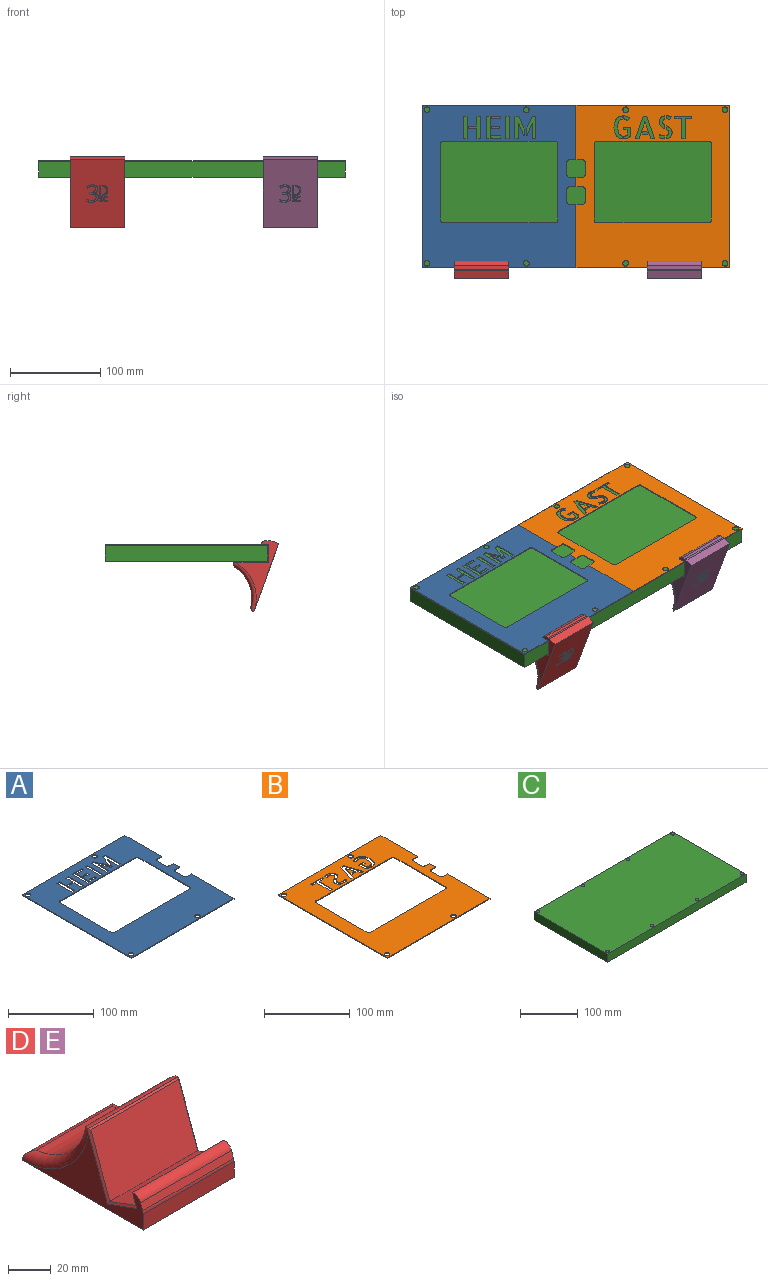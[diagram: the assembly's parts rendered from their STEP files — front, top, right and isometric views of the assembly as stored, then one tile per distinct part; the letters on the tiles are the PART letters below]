
ASSEMBLY  parts=5 mates=4
PART A: 78 faces, bbox 170x180x1 mm
  f0: plane 4.07x1mm, normal (0,-1,0), area 4.1mm2, adj f1,f67,f68,f69
  f1: plane 24.99x1mm, normal (-1,0,0), area 25mm2, adj f0,f2,f68,f69
  f2: plane 4.07x1mm, normal (0,1,0), area 4.1mm2, adj f1,f3,f68,f69
  f3: plane 11.26x1mm, normal (1,0,0), area 11.3mm2, adj f2,f4,f68,f69
  f4: plane 9.43x1mm, normal (0,1,0), area 9.4mm2, adj f3,f5,f68,f69
  f5: plane 2.78x1mm, normal (1,0,0), area 2.8mm2, adj f4,f6,f68,f69
  f6: plane 9.43x1mm, normal (0,-1,0), area 9.4mm2, adj f5,f67,f68,f69
  f7: plane 24.99x1mm, normal (1,0,0), area 25mm2, adj f8,f53,f68,f69
  f8: plane 4.13x1mm, normal (0,-1,0), area 4.1mm2, adj f7,f9,f68,f69
  f9: plane 24.99x1mm, normal (-1,0,0), area 25mm2, adj f8,f53,f68,f69
  f10: plane 24.99x1mm, normal (1,0,0), area 25mm2, adj f11,f54,f68,f69
  f11: plane 4.13x1mm, normal (0,-1,0), area 4.1mm2, adj f10,f12,f68,f69
  f12: plane 24.99x1mm, normal (-1,0,0), area 25mm2, adj f11,f54,f68,f69
  f13: plane 2.78x1mm, normal (-1,0,0), area 2.8mm2, adj f14,f55,f68,f69
  f14: plane 9.05x1mm, normal (0,1,0), area 9mm2, adj f13,f15,f68,f69
  f15: plane 2.78x1mm, normal (1,0,0), area 2.8mm2, adj f14,f55,f68,f69
  f16: plane 3.09x1mm, normal (1,0,0), area 3.1mm2, adj f17,f56,f68,f69
  f17: plane 10.1x1mm, normal (0,-1,0), area 10.1mm2, adj f16,f18,f68,f69
  f18: plane 3.09x1mm, normal (-1,0,0), area 3.1mm2, adj f17,f56,f68,f69
  f19: plane 10.1x1mm, normal (0,-1,0), area 10.1mm2, adj f20,f57,f68,f69
  f20: plane 3.08x1mm, normal (-1,0,0), area 3.1mm2, adj f19,f21,f68,f69
  f21: plane 10.1x1mm, normal (0,1,0), area 10.1mm2, adj f20,f57,f68,f69
  f22: plane 24.99x1mm, normal (-1,0,0), area 25mm2, adj f23,f58,f68,f69
  f23: plane 4.13x1mm, normal (0,1,0), area 4.1mm2, adj f22,f24,f68,f69
  f24: plane 24.99x1mm, normal (1,0,0), area 25mm2, adj f23,f58,f68,f69
  f25: plane 24.99x1mm, normal (1,0,0), area 25mm2, adj f26,f59,f68,f69
  f26: plane 4.14x1mm, normal (0,-1,0), area 4.1mm2, adj f25,f27,f68,f69
  f27: plane 15.42x6.71mm, normal (-0.92,-0.4,0), area 16.8mm2, adj f26,f28,f68,f69
  f28: plane 6.28x1mm, normal (-1,0,0), area 6.3mm2, adj f27,f29,f68,f69
  f29: plane 1.09x1mm, normal (0,1,0), area 1.1mm2, adj f28,f30,f68,f69
  f30: plane 13.91x5.63mm, normal (0.93,0.38,0), area 15mm2, adj f29,f31,f68,f69
  f31: plane 17.19x1mm, normal (-1,0,0), area 17.2mm2, adj f30,f59,f68,f69
  f32: plane 15.49x6.72mm, normal (0.92,-0.4,0), area 16.9mm2, adj f33,f60,f68,f69
  f33: plane 4.13x1mm, normal (0,-1,0), area 4.1mm2, adj f32,f34,f68,f69
  f34: plane 24.99x1mm, normal (-1,0,0), area 25mm2, adj f33,f35,f68,f69
  f35: plane 4.13x1mm, normal (0,1,0), area 4.1mm2, adj f34,f36,f68,f69
  f36: plane 17.19x1mm, normal (1,0,0), area 17.2mm2, adj f35,f37,f68,f69
  f37: plane 13.91x5.59mm, normal (-0.93,0.37,0), area 15mm2, adj f36,f38,f68,f69
  f38: plane 1.12x1mm, normal (0,1,0), area 1.1mm2, adj f37,f60,f68,f69
  f39: plane 60x1mm, normal (1,0,0), area 60mm2, adj f40,f65,f68,f69
  f40: plane 170x1mm, normal (0,1,0), area 170mm2, adj f39,f41,f68,f69
  f41: plane 180x1mm, normal (-1,0,0), area 180mm2, adj f40,f42,f68,f69
  f42: plane 170x1mm, normal (0,-1,0), area 170mm2, adj f41,f43,f68,f69
  f43: plane 70x1mm, normal (1,0,0), area 70mm2, adj f42,f44,f68,f69
  f44: plane 7x1mm, normal (0,1,0), area 7mm2, adj f43,f68,f69,f74
  f45: plane 14x1mm, normal (1,0,0), area 14mm2, adj f68,f69,f74,f75
  f46: plane 7x1mm, normal (0,-1,0), area 7mm2, adj f47,f68,f69,f75
  f47: plane 10x1mm, normal (1,0,0), area 10mm2, adj f46,f48,f68,f69
  f48: plane 7x1mm, normal (0,1,0), area 7mm2, adj f47,f68,f69,f76
  f49: plane 14x1mm, normal (1,0,0), area 14mm2, adj f68,f69,f76,f77
  f50: plane 84x1mm, normal (1,0,0), area 84mm2, adj f68,f69,f70,f73
  f51: plane 124x1mm, normal (0,-1,0), area 124mm2, adj f68,f69,f70,f71
  f52: plane 84x1mm, normal (-1,0,0), area 84mm2, adj f68,f69,f71,f72
  f53: plane 4.13x1mm, normal (0,1,0), area 4.1mm2, adj f7,f9,f68,f69
  f54: plane 4.13x1mm, normal (0,1,0), area 4.1mm2, adj f10,f12,f68,f69
  f55: plane 9.05x1mm, normal (0,-1,0), area 9mm2, adj f13,f15,f68,f69
  f56: plane 10.1x1mm, normal (0,1,0), area 10.1mm2, adj f16,f18,f68,f69
  f57: plane 3.08x1mm, normal (1,0,0), area 3.1mm2, adj f19,f21,f68,f69
  f58: plane 4.13x1mm, normal (0,-1,0), area 4.1mm2, adj f22,f24,f68,f69
  f59: plane 4.14x1mm, normal (0,1,0), area 4.1mm2, adj f25,f31,f68,f69
  f60: plane 6.21x1mm, normal (1,0,0), area 6.2mm2, adj f32,f38,f68,f69
  f61: cylinder r=3.25mm len=6.5mm, axis (0,0,-1), area 20.4mm2, adj f68,f69
  f62: cylinder r=3.25mm len=6.5mm, axis (0,0,-1), area 20.4mm2, adj f68,f69
  f63: cylinder r=3.25mm len=6.5mm, axis (0,0,-1), area 20.4mm2, adj f68,f69
  f64: cylinder r=3.25mm len=6.5mm, axis (0,0,-1), area 20.4mm2, adj f68,f69
  f65: plane 7x1mm, normal (0,-1,0), area 7mm2, adj f39,f68,f69,f77
  f66: plane 124x1mm, normal (0,1,0), area 124mm2, adj f68,f69,f72,f73
  f67: plane 10.95x1mm, normal (1,0,0), area 10.9mm2, adj f0,f6,f68,f69
  f68: plane 180x170mm, normal (0,0,1), area 17541mm2, adj f0,f1,f2,f3,f4,f5,f6,f7
  f69: plane 180x170mm, normal (0,0,-1), area 17541mm2, adj f0,f1,f2,f3,f4,f5,f6,f7
  f70: cylinder r=3mm len=3mm, axis (0,0,-1), area 4.7mm2, adj f50,f51,f68,f69
  f71: cylinder r=3mm len=3mm, axis (0,0,1), area 4.7mm2, adj f51,f52,f68,f69
  f72: cylinder r=3mm len=3mm, axis (0,0,-1), area 4.7mm2, adj f52,f66,f68,f69
  f73: cylinder r=3mm len=3mm, axis (0,0,1), area 4.7mm2, adj f50,f66,f68,f69
  f74: cylinder r=3mm len=3mm, axis (0,0,1), area 4.7mm2, adj f44,f45,f68,f69
  f75: cylinder r=3mm len=3mm, axis (0,0,-1), area 4.7mm2, adj f45,f46,f68,f69
  f76: cylinder r=3mm len=3mm, axis (0,0,1), area 4.7mm2, adj f48,f49,f68,f69
  f77: cylinder r=3mm len=3mm, axis (0,0,-1), area 4.7mm2, adj f49,f65,f68,f69
PART B: 140 faces, bbox 170x180x1 mm
  f0: plane 14x1mm, normal (1,0,0), area 14mm2, adj f130,f131,f136,f139
  f1: plane 7x1mm, normal (0,-1,0), area 7mm2, adj f2,f130,f131,f136
  f2: plane 60x1mm, normal (1,0,0), area 60mm2, adj f1,f3,f130,f131
  f3: plane 170x1mm, normal (0,1,0), area 170mm2, adj f2,f4,f130,f131
  f4: plane 180x1mm, normal (-1,0,0), area 180mm2, adj f3,f5,f130,f131
  f5: plane 170x1mm, normal (0,-1,0), area 170mm2, adj f4,f6,f130,f131
  f6: plane 70x1mm, normal (1,0,0), area 70mm2, adj f5,f7,f130,f131
  f7: plane 7x1mm, normal (0,1,0), area 7mm2, adj f6,f130,f131,f137
  f8: plane 14x1mm, normal (1,0,0), area 14mm2, adj f130,f131,f137,f138
  f9: plane 7x1mm, normal (0,-1,0), area 7mm2, adj f10,f130,f131,f138
  f10: plane 10x1mm, normal (1,0,0), area 10mm2, adj f9,f129,f130,f131
  f11: plane 2.78x1mm, normal (1,0,0), area 2.8mm2, adj f12,f118,f130,f131
  f12: plane 19.02x1mm, normal (0,-1,0), area 19mm2, adj f11,f13,f130,f131
  f13: plane 2.78x1mm, normal (-1,0,0), area 2.8mm2, adj f12,f14,f130,f131
  f14: plane 7.46x1mm, normal (0,1,0), area 7.5mm2, adj f13,f15,f130,f131
  f15: plane 22.21x1mm, normal (-1,0,0), area 22.2mm2, adj f14,f16,f130,f131
  f16: plane 4.1x1mm, normal (0,1,0), area 4.1mm2, adj f15,f17,f130,f131
  f17: plane 22.21x1mm, normal (1,0,0), area 22.2mm2, adj f16,f118,f130,f131
  f18: extruded ~2.29x1.09mm, area 2.5mm2, adj f19,f119,f130,f131
  f19: plane 3.97x1mm, normal (-1,0,0), area 4mm2, adj f18,f20,f130,f131
  f20: extruded ~2x1.46mm, area 2.5mm2, adj f19,f21,f130,f131
  f21: extruded ~1.97x1mm, area 2.2mm2, adj f20,f22,f130,f131
  f22: extruded ~3.69x2.78mm, area 5.1mm2, adj f21,f23,f130,f131
  f23: plane 3.26x1mm, normal (-1,0,0), area 3.3mm2, adj f22,f24,f130,f131
  f24: extruded ~2.78x1mm, area 2.9mm2, adj f23,f25,f130,f131
  f25: extruded ~2.05x1.58mm, area 2.6mm2, adj f24,f26,f130,f131
  f26: extruded ~2.09x1.29mm, area 2.5mm2, adj f25,f27,f130,f131
  f27: extruded ~2.37x1mm, area 2.4mm2, adj f26,f28,f130,f131
  f28: extruded ~2.95x1mm, area 3mm2, adj f27,f29,f130,f131
  f29: extruded ~2.02x1.56mm, area 2.6mm2, adj f28,f119,f130,f131
  f30: extruded ~1.2x1mm, area 1.3mm2, adj f31,f120,f130,f131
  f31: plane 2.92x1mm, normal (-0.97,-0.24,0), area 3mm2, adj f30,f32,f130,f131
  f32: extruded ~1.38x1mm, area 1.6mm2, adj f31,f33,f130,f131
  f33: extruded ~1.68x1mm, area 1.8mm2, adj f32,f34,f130,f131
  f34: extruded ~1.75x1mm, area 1.8mm2, adj f33,f35,f130,f131
  f35: extruded ~1.68x1mm, area 1.7mm2, adj f34,f36,f130,f131
  f36: plane 1x0.07mm, normal (0,1,0), area 0.1mm2, adj f35,f37,f130,f131
  f37: plane 3.22x1mm, normal (1,0,0), area 3.2mm2, adj f36,f38,f130,f131
  f38: plane 1x0.1mm, normal (0,-1,0), area 0.1mm2, adj f37,f39,f130,f131
  f39: extruded ~1.46x1mm, area 1.5mm2, adj f38,f40,f130,f131
  f40: extruded ~1.56x1mm, area 1.6mm2, adj f39,f120,f130,f131
  f41: extruded ~2.68x1mm, area 2.7mm2, adj f42,f121,f130,f131
  f42: extruded ~2.68x1mm, area 2.8mm2, adj f41,f43,f130,f131
  f43: extruded ~1.97x1.51mm, area 2.5mm2, adj f42,f44,f130,f131
  f44: extruded ~2.03x1.48mm, area 2.5mm2, adj f43,f45,f130,f131
  f45: extruded ~2.24x1.17mm, area 2.5mm2, adj f44,f46,f130,f131
  f46: plane 3.87x1mm, normal (1,0,0), area 3.9mm2, adj f45,f47,f130,f131
  f47: extruded ~1.8x1.42mm, area 2.3mm2, adj f46,f48,f130,f131
  f48: extruded ~2.14x1mm, area 2.3mm2, adj f47,f49,f130,f131
  f49: extruded ~1.88x1mm, area 2.1mm2, adj f48,f50,f130,f131
  f50: extruded ~1.8x1.3mm, area 2.3mm2, adj f49,f51,f130,f131
  f51: plane 3.56x1mm, normal (1,0,0), area 3.6mm2, adj f50,f52,f130,f131
  f52: extruded ~2.46x1mm, area 2.6mm2, adj f51,f53,f130,f131
  f53: extruded ~2.03x1.42mm, area 2.5mm2, adj f52,f121,f130,f131
  f54: extruded ~1x0.41mm, area 0.5mm2, adj f55,f122,f130,f131
  f55: extruded ~1x0.34mm, area 0.4mm2, adj f54,f56,f130,f131
  f56: extruded ~1x0.76mm, area 0.9mm2, adj f55,f57,f130,f131
  f57: extruded ~1x0.98mm, area 1.1mm2, adj f56,f58,f130,f131
  f58: extruded ~1x0.97mm, area 1.1mm2, adj f57,f59,f130,f131
  f59: extruded ~2.49x1mm, area 2.7mm2, adj f58,f60,f130,f131
  f60: extruded ~3.04x1mm, area 3.1mm2, adj f59,f61,f130,f131
  f61: plane 3.42x1mm, normal (-1,0,0), area 3.4mm2, adj f60,f62,f130,f131
  f62: extruded ~1.73x1mm, area 1.7mm2, adj f61,f63,f130,f131
  f63: extruded ~1.12x1mm, area 1.1mm2, adj f62,f122,f130,f131
  f64: plane 2.75x1mm, normal (0.94,-0.34,0), area 2.9mm2, adj f65,f123,f130,f131
  f65: plane 4.55x1mm, normal (0,-1,0), area 4.5mm2, adj f64,f66,f130,f131
  f66: plane 2.75x1mm, normal (-0.95,-0.33,0), area 2.9mm2, adj f65,f123,f130,f131
  f67: plane 4.2x1mm, normal (0,1,0), area 4.2mm2, adj f68,f124,f130,f131
  f68: plane 24.96x8.68mm, normal (0.94,-0.33,0), area 26.4mm2, adj f67,f69,f130,f131
  f69: plane 4.04x1mm, normal (0,-1,0), area 4mm2, adj f68,f70,f130,f131
  f70: plane 24.96x8.75mm, normal (-0.94,-0.33,0), area 26.4mm2, adj f69,f71,f130,f131
  f71: plane 4.24x1mm, normal (0,1,0), area 4.2mm2, adj f70,f72,f130,f131
  f72: plane 18.72x6.54mm, normal (0.94,0.33,0), area 19.8mm2, adj f71,f124,f130,f131
  f73: plane 9.66x1mm, normal (1,0,0), area 9.7mm2, adj f74,f125,f130,f131
  f74: plane 8.27x1mm, normal (0,-1,0), area 8.3mm2, adj f73,f75,f130,f131
  f75: plane 2.78x1mm, normal (-1,0,0), area 2.8mm2, adj f74,f76,f130,f131
  f76: plane 4.24x1mm, normal (0,1,0), area 4.2mm2, adj f75,f77,f130,f131
  f77: plane 6.17x1mm, normal (-1,0,0), area 6.2mm2, adj f76,f78,f130,f131
  f78: extruded ~1x0.83mm, area 1mm2, adj f77,f79,f130,f131
  f79: extruded ~1.19x1mm, area 1.2mm2, adj f78,f80,f130,f131
  f80: extruded ~1.22x1mm, area 1.2mm2, adj f79,f81,f130,f131
  f81: extruded ~1x1mm, area 1mm2, adj f80,f82,f130,f131
  f82: plane 2.98x1mm, normal (-1,0,0), area 3mm2, adj f81,f83,f130,f131
  f83: plane 1x0.04mm, normal (0,1,0), area 0mm2, adj f82,f84,f130,f131
  f84: extruded ~2.25x1mm, area 2.3mm2, adj f83,f85,f130,f131
  f85: extruded ~2.2x1mm, area 2.3mm2, adj f84,f86,f130,f131
  f86: extruded ~2.03x1.04mm, area 2.3mm2, adj f85,f125,f130,f131
  f87: extruded ~5.17x1mm, area 5.2mm2, adj f88,f126,f130,f131
  f88: extruded ~5.17x1mm, area 5.2mm2, adj f87,f89,f130,f131
  f89: extruded ~3.85x1.86mm, area 4.3mm2, adj f88,f90,f130,f131
  f90: extruded ~2.85x2.53mm, area 3.8mm2, adj f89,f91,f130,f131
  f91: extruded ~3.59x1.17mm, area 3.8mm2, adj f90,f92,f130,f131
  f92: plane 3.09x1mm, normal (1,0,0), area 3.1mm2, adj f91,f93,f130,f131
  f93: extruded ~1.88x1mm, area 2.1mm2, adj f92,f94,f130,f131
  f94: extruded ~1.92x1.53mm, area 2.5mm2, adj f93,f95,f130,f131
  f95: extruded ~2.86x1.03mm, area 3.1mm2, adj f94,f96,f130,f131
  f96: extruded ~3.87x1mm, area 3.9mm2, adj f95,f97,f130,f131
  f97: extruded ~3.81x1mm, area 3.8mm2, adj f96,f98,f130,f131
  f98: extruded ~2.75x1.03mm, area 2.9mm2, adj f97,f99,f130,f131
  f99: extruded ~1.78x1.53mm, area 2.4mm2, adj f98,f100,f130,f131
  f100: extruded ~1.88x1mm, area 2.1mm2, adj f99,f101,f130,f131
  f101: plane 3.39x1mm, normal (1,0,0), area 3.4mm2, adj f100,f102,f130,f131
  f102: extruded ~3.59x1.15mm, area 3.8mm2, adj f101,f103,f130,f131
  f103: extruded ~2.85x2.49mm, area 3.8mm2, adj f102,f126,f130,f131
  f104: extruded ~1.86x1.42mm, area 2.4mm2, adj f105,f127,f130,f131
  f105: plane 2.82x2.51mm, normal (0.66,0.75,0), area 3.8mm2, adj f104,f106,f130,f131
  f106: extruded ~3.15x2.03mm, area 3.8mm2, adj f105,f107,f130,f131
  f107: extruded ~3.8x1mm, area 3.9mm2, adj f106,f108,f130,f131
  f108: plane 1x0.04mm, normal (0,-1,0), area 0mm2, adj f107,f109,f130,f131
  f109: plane 3.35x1mm, normal (-1,0,0), area 3.4mm2, adj f108,f110,f130,f131
  f110: plane 1x0.14mm, normal (0,1,0), area 0.1mm2, adj f109,f127,f130,f131
  f111: plane 84x1mm, normal (1,0,0), area 84mm2, adj f130,f131,f132,f135
  f112: plane 124x1mm, normal (0,-1,0), area 124mm2, adj f130,f131,f132,f133
  f113: plane 84x1mm, normal (-1,0,0), area 84mm2, adj f130,f131,f133,f134
  f114: cylinder r=3.25mm len=6.5mm, axis (0,0,-1), area 20.4mm2, adj f130,f131
  f115: cylinder r=3.25mm len=6.5mm, axis (0,0,-1), area 20.4mm2, adj f130,f131
  f116: cylinder r=3.25mm len=6.5mm, axis (0,0,-1), area 20.4mm2, adj f130,f131
  f117: cylinder r=3.25mm len=6.5mm, axis (0,0,-1), area 20.4mm2, adj f130,f131
  f118: plane 7.46x1mm, normal (0,1,0), area 7.5mm2, adj f11,f17,f130,f131
  f119: extruded ~2.12x1.41mm, area 2.6mm2, adj f18,f29,f130,f131
  f120: extruded ~1.51x1mm, area 1.6mm2, adj f30,f40,f130,f131
  f121: extruded ~2.09x1.37mm, area 2.5mm2, adj f41,f53,f130,f131
  f122: extruded ~1x0.68mm, area 0.8mm2, adj f54,f63,f130,f131
  f123: plane 6.48x1mm, normal (0,1,0), area 6.5mm2, adj f64,f66,f130,f131
  f124: plane 18.72x6.48mm, normal (-0.95,0.33,0), area 19.8mm2, adj f67,f72,f130,f131
  f125: extruded ~1.74x1.61mm, area 2.4mm2, adj f73,f86,f130,f131
  f126: extruded ~3.83x1.86mm, area 4.3mm2, adj f87,f103,f130,f131
  f127: extruded ~2.17x1mm, area 2.2mm2, adj f104,f110,f130,f131
  f128: plane 124x1mm, normal (0,1,0), area 124mm2, adj f130,f131,f134,f135
  f129: plane 7x1mm, normal (0,1,0), area 7mm2, adj f10,f130,f131,f139
  f130: plane 180x170mm, normal (0,0,1), area 17678.5mm2, adj f0,f1,f2,f3,f4,f5,f6,f7
  f131: plane 180x170mm, normal (0,0,-1), area 17678.5mm2, adj f0,f1,f2,f3,f4,f5,f6,f7
  f132: cylinder r=3mm len=3mm, axis (0,0,-1), area 4.7mm2, adj f111,f112,f130,f131
  f133: cylinder r=3mm len=3mm, axis (0,0,1), area 4.7mm2, adj f112,f113,f130,f131
  f134: cylinder r=3mm len=3mm, axis (0,0,-1), area 4.7mm2, adj f113,f128,f130,f131
  f135: cylinder r=3mm len=3mm, axis (0,0,1), area 4.7mm2, adj f111,f128,f130,f131
  f136: cylinder r=3mm len=3mm, axis (0,0,-1), area 4.7mm2, adj f0,f1,f130,f131
  f137: cylinder r=3mm len=3mm, axis (0,0,1), area 4.7mm2, adj f7,f8,f130,f131
  f138: cylinder r=3mm len=3mm, axis (0,0,-1), area 4.7mm2, adj f8,f9,f130,f131
  f139: cylinder r=3mm len=3mm, axis (0,0,1), area 4.7mm2, adj f0,f129,f130,f131
PART C: 22 faces, bbox 340x180x18.5 mm
  f0: plane 340x17.5mm, normal (0,1,0), area 5950mm2, adj f1,f3,f4,f5
  f1: plane 180x17.5mm, normal (-1,0,0), area 3150mm2, adj f0,f2,f4,f5
  f2: plane 340x17.5mm, normal (0,-1,0), area 5950mm2, adj f1,f3,f4,f5
  f3: plane 180x17.5mm, normal (1,0,0), area 3150mm2, adj f0,f2,f4,f5
  f4: plane 340x180mm, normal (0,0,1), area 60973.8mm2, adj f0,f1,f2,f3,f6,f8,f10,f12
  f5: plane 340x180mm, normal (0,0,-1), area 61200mm2, adj f0,f1,f2,f3
  f6: cylinder r=3mm len=6mm, axis (0,0,-1), area 18.8mm2, adj f4,f7
  f7: plane 6x6mm, normal (0,0,1), area 28.3mm2, adj f6
  f8: cylinder r=3mm len=6mm, axis (0,0,-1), area 18.8mm2, adj f4,f9
  f9: plane 6x6mm, normal (0,0,1), area 28.3mm2, adj f8
  f10: cylinder r=3mm len=6mm, axis (0,0,-1), area 18.8mm2, adj f4,f11
  f11: plane 6x6mm, normal (0,0,1), area 28.3mm2, adj f10
  f12: cylinder r=3mm len=6mm, axis (0,0,-1), area 18.8mm2, adj f4,f13
  f13: plane 6x6mm, normal (0,0,1), area 28.3mm2, adj f12
  f14: cylinder r=3mm len=6mm, axis (0,0,-1), area 18.8mm2, adj f4,f15
  f15: plane 6x6mm, normal (0,0,1), area 28.3mm2, adj f14
  f16: cylinder r=3mm len=6mm, axis (0,0,-1), area 18.8mm2, adj f4,f17
  f17: plane 6x6mm, normal (0,0,1), area 28.3mm2, adj f16
  f18: cylinder r=3mm len=6mm, axis (0,0,-1), area 18.8mm2, adj f4,f19
  f19: plane 6x6mm, normal (0,0,1), area 28.3mm2, adj f18
  f20: cylinder r=3mm len=6mm, axis (0,0,-1), area 18.8mm2, adj f4,f21
  f21: plane 6x6mm, normal (0,0,1), area 28.3mm2, adj f20
PART D: 114 faces, bbox 60x80.1x47.6 mm
  f0: plane 80x60mm, normal (0,0,-1), area 4595.9mm2, adj f7,f8,f9,f10,f12,f13,f27,f28
  f1: cylinder r=40mm len=50mm, axis (-1,0,0), area 2432.8mm2, adj f11,f12,f13,f14
  f2: plane 59x0.16mm, normal (0,0,1), area 9.2mm2, adj f14,f22,f24,f26
  f3: plane 58.01x34.54mm, normal (0,-0.94,0.34), area 2131.4mm2, adj f4,f20,f22,f24,f25,f26
  f4: plane 58x17.38mm, normal (0,0.34,0.94), area 1073mm2, adj f3,f5,f18,f23
  f5: plane 58x5.94mm, normal (0,0.94,-0.34), area 366.7mm2, adj f4,f17,f19,f21
  f6: plane 60x3.87mm, normal (0,-0.94,0.34), area 247.1mm2, adj f9,f10,f15,f16
  f7: plane 60x9.12mm, normal (0,-1,0), area 547.1mm2, adj f0,f9,f10,f16
  f8: plane 60x0.32mm, normal (0,1,0), area 19.3mm2, adj f0,f11,f12,f13
  f9: plane 79.98x37.39mm, normal (1,0,0), area 862.6mm2, adj f0,f6,f7,f12,f15,f16,f17,f18
  f10: plane 79.98x37.38mm, normal (-1,0,0), area 862.6mm2, adj f0,f6,f7,f13,f15,f16,f19,f21
  f11: cylinder r=5mm len=59.98mm, axis (-1,0,0), area 398.9mm2, adj f1,f8,f12,f13
  f12: torus R=45mm, axis (1,0,0), area 446.6mm2, adj f0,f1,f8,f9,f11,f14,f22
  f13: torus R=45mm, axis (1,0,0), area 446.6mm2, adj f0,f1,f8,f10,f11,f14,f26
  f14: cylinder r=5mm len=59.63mm, axis (-1,0,0), area 373.7mm2, adj f1,f2,f12,f13,f22,f26
  f15: cylinder r=5mm len=60mm, axis (-1,0,0), area 395.4mm2, adj f6,f9,f10,f19
  f16: cylinder r=5mm len=60mm, axis (-1,0,0), area 104.7mm2, adj f6,f7,f9,f10
  f17: plane 7.61x3.44mm, normal (0.71,0.66,-0.24), area 10.2mm2, adj f5,f9,f18,f19
  f18: plane 19.26x7.61mm, normal (0.71,0.24,0.66), area 27.6mm2, adj f4,f9,f17,f20
  f19: plane 60x1.34mm, normal (0,0.85,0.53), area 93.6mm2, adj f5,f9,f10,f15,f17,f21
  f20: plane 34.65x13.08mm, normal (0.71,-0.66,0.24), area 50.9mm2, adj f3,f9,f18,f22
  f21: plane 7.61x3.44mm, normal (-0.71,0.66,-0.24), area 10.2mm2, adj f5,f10,f19,f23
  f22: bspline ~2.45x1.97mm, area 2.9mm2, adj f2,f3,f12,f14,f20,f24
  f23: plane 19.26x7.61mm, normal (-0.71,0.24,0.66), area 27.6mm2, adj f4,f10,f21,f25
  f24: plane 58.8x0.96mm, normal (0,-0.57,0.82), area 67mm2, adj f2,f3,f22,f26
  f25: plane 34.65x13.08mm, normal (-0.71,-0.66,0.24), area 50.9mm2, adj f3,f10,f23,f26
  f26: bspline ~2.45x1.97mm, area 2.9mm2, adj f2,f3,f13,f14,f24,f25
  f27: extruded ~1.23x0.57mm, area 0.7mm2, adj f0,f28,f51,f52
  f28: extruded ~0.99x0.5mm, area 0.5mm2, adj f0,f27,f29,f52
  f29: extruded ~1.29x0.72mm, area 0.7mm2, adj f0,f28,f30,f52
  f30: extruded ~0.83x0.5mm, area 0.5mm2, adj f0,f29,f31,f52
  f31: extruded ~0.5x0.38mm, area 0.3mm2, adj f0,f30,f32,f52
  f32: extruded ~0.51x0.5mm, area 0.3mm2, adj f0,f31,f33,f52
  f33: extruded ~0.66x0.5mm, area 0.4mm2, adj f0,f32,f34,f52
  f34: extruded ~0.86x0.5mm, area 0.5mm2, adj f0,f33,f35,f52
  f35: extruded ~1.43x0.5mm, area 0.7mm2, adj f0,f34,f36,f52
  f36: plane 0.6x0.5mm, normal (-0.94,-0.34,0), area 0.3mm2, adj f0,f35,f37,f52
  f37: extruded ~1.63x0.5mm, area 0.8mm2, adj f0,f36,f38,f52
  f38: extruded ~1.37x0.5mm, area 0.7mm2, adj f0,f37,f39,f52
  f39: extruded ~1.09x0.52mm, area 0.6mm2, adj f0,f38,f40,f52
  f40: extruded ~1.06x0.5mm, area 0.6mm2, adj f0,f39,f41,f52
  f41: extruded ~1.19x0.7mm, area 0.7mm2, adj f0,f40,f42,f52
  f42: extruded ~0.88x0.5mm, area 0.5mm2, adj f0,f41,f43,f52
  f43: extruded ~0.5x0.42mm, area 0.3mm2, adj f0,f42,f44,f52
  f44: extruded ~0.51x0.5mm, area 0.3mm2, adj f0,f43,f45,f52
  f45: extruded ~0.73x0.5mm, area 0.4mm2, adj f0,f44,f46,f52
  f46: extruded ~1.04x0.5mm, area 0.5mm2, adj f0,f45,f47,f52
  f47: extruded ~0.85x0.5mm, area 0.4mm2, adj f0,f46,f48,f52
  f48: extruded ~0.8x0.5mm, area 0.4mm2, adj f0,f47,f49,f52
  f49: plane 0.67x0.5mm, normal (1,0,0), area 0.3mm2, adj f0,f48,f50,f52
  f50: extruded ~1.63x0.5mm, area 0.8mm2, adj f0,f49,f51,f52
  f51: extruded ~1.55x0.5mm, area 0.8mm2, adj f0,f27,f50,f52
  f52: plane 6.12x3.74mm, normal (0,0,-1), area 8.2mm2, adj f27,f28,f29,f30,f31,f32,f33,f34
  f53: extruded ~3.45x1.15mm, area 1.9mm2, adj f54,f66,f67,f113
  f54: extruded ~3.54x1.22mm, area 1.9mm2, adj f53,f55,f67,f113
  f55: extruded ~3.66x1.2mm, area 2mm2, adj f54,f56,f67,f113
  f56: plane 1.66x0.5mm, normal (0,1,0), area 0.8mm2, adj f55,f57,f67,f113
  f57: plane 9.34x0.5mm, normal (-1,0,0), area 4.7mm2, adj f56,f58,f67,f113
  f58: plane 1.98x0.5mm, normal (0,-1,0), area 1mm2, adj f57,f66,f67,f113
  f59: extruded ~4.43x1.57mm, area 2.4mm2, adj f0,f60,f65,f67
  f60: extruded ~4.22x1.51mm, area 2.3mm2, adj f0,f59,f61,f67
  f61: extruded ~4.24x1.51mm, area 2.3mm2, adj f0,f60,f62,f67
  f62: plane 3.58x0.5mm, normal (0,1,0), area 1.8mm2, adj f0,f61,f63,f67
  f63: plane 11.69x0.5mm, normal (1,0,0), area 5.8mm2, adj f0,f62,f64,f67
  f64: plane 3.24x0.5mm, normal (0,-1,0), area 1.6mm2, adj f0,f63,f65,f67
  f65: extruded ~4.52x1.53mm, area 2.4mm2, adj f0,f59,f64,f67
  f66: extruded ~3.41x1.16mm, area 1.9mm2, adj f53,f58,f67,f113
  f67: plane 11.69x9.33mm, normal (0,0,-1), area 43.2mm2, adj f53,f54,f55,f56,f57,f58,f59,f60
  f68: extruded ~1.55x0.65mm, area 0.9mm2, adj f0,f69,f82,f83
  f69: extruded ~1.35x0.5mm, area 0.7mm2, adj f0,f68,f70,f83
  f70: plane 0.59x0.5mm, normal (-0.9,-0.44,0), area 0.3mm2, adj f0,f69,f71,f83
  f71: extruded ~1.64x0.5mm, area 0.8mm2, adj f0,f70,f72,f83
  f72: extruded ~1.53x0.5mm, area 0.8mm2, adj f0,f71,f73,f83
  f73: extruded ~1.07x0.99mm, area 0.7mm2, adj f0,f72,f74,f83
  f74: extruded ~1.61x0.5mm, area 0.8mm2, adj f0,f73,f75,f83
  f75: extruded ~2.27x0.71mm, area 1.2mm2, adj f0,f74,f76,f83
  f76: extruded ~2.03x0.8mm, area 1.1mm2, adj f0,f75,f77,f83
  f77: extruded ~1.53x0.5mm, area 0.8mm2, adj f0,f76,f78,f83
  f78: plane 0.61x0.5mm, normal (-1,0,0), area 0.3mm2, adj f0,f77,f79,f83
  f79: extruded ~1.42x0.5mm, area 0.7mm2, adj f0,f78,f80,f83
  f80: extruded ~1.56x0.64mm, area 0.9mm2, adj f0,f79,f81,f83
  f81: extruded ~1.8x0.55mm, area 1mm2, adj f0,f80,f82,f83
  f82: extruded ~1.79x0.57mm, area 1mm2, adj f0,f68,f81,f83
  f83: plane 6.12x4.5mm, normal (0,0,-1), area 7.7mm2, adj f68,f69,f70,f71,f72,f73,f74,f75
  f84: extruded ~3.11x1.07mm, area 1.7mm2, adj f0,f85,f111,f112
  f85: extruded ~3.63x1.6mm, area 2.1mm2, adj f0,f84,f86,f112
  f86: extruded ~4.49x1.32mm, area 2.4mm2, adj f0,f85,f87,f112
  f87: extruded ~3.36x0.55mm, area 1.7mm2, adj f0,f86,f88,f112
  f88: extruded ~2.81x1.51mm, area 1.6mm2, adj f0,f87,f89,f112
  f89: plane 1.52x1.14mm, normal (0.8,-0.6,0), area 0.9mm2, adj f0,f88,f90,f112
  f90: extruded ~2.63x1.3mm, area 1.5mm2, adj f0,f89,f91,f112
  f91: extruded ~2.45x0.5mm, area 1.2mm2, adj f0,f90,f92,f112
  f92: extruded ~2.71x0.83mm, area 1.4mm2, adj f0,f91,f93,f112
  f93: extruded ~2.28x1mm, area 1.3mm2, adj f0,f92,f94,f112
  f94: extruded ~2.84x1.36mm, area 1.6mm2, adj f0,f93,f95,f112
  f95: extruded ~3.67x1.02mm, area 1.9mm2, adj f0,f94,f96,f112
  f96: plane 1.98x0.5mm, normal (0,1,0), area 1mm2, adj f0,f95,f97,f112
  f97: plane 1.94x0.5mm, normal (1,0,0), area 1mm2, adj f0,f96,f98,f112
  f98: plane 1.95x0.5mm, normal (0,-1,0), area 1mm2, adj f0,f97,f99,f112
  f99: extruded ~5.67x3.61mm, area 3.8mm2, adj f0,f98,f100,f112
  f100: extruded ~5.14x4.03mm, area 3.7mm2, adj f0,f99,f101,f112
  f101: extruded ~2.76x0.5mm, area 1.4mm2, adj f0,f100,f102,f112
  f102: extruded ~2.75x0.97mm, area 1.5mm2, adj f0,f101,f103,f112
  f103: plane 2.14x0.5mm, normal (1,0,0), area 1.1mm2, adj f0,f102,f104,f112
  f104: extruded ~2.54x0.83mm, area 1.3mm2, adj f0,f103,f105,f112
  f105: extruded ~2.88x0.5mm, area 1.4mm2, adj f0,f104,f106,f112
  f106: extruded ~5.59x1.53mm, area 2.9mm2, adj f0,f105,f107,f112
  f107: extruded ~4.36x1.97mm, area 2.5mm2, adj f0,f106,f108,f112
  f108: extruded ~3.2x1.15mm, area 1.7mm2, adj f0,f107,f109,f112
  f109: extruded ~3.54x1.52mm, area 2mm2, adj f0,f108,f110,f112
  f110: plane 0.5x0.11mm, normal (-1,0,0), area 0.1mm2, adj f0,f109,f111,f112
  f111: extruded ~3.02x1.61mm, area 1.7mm2, adj f0,f84,f110,f112
  f112: plane 20.39x12.98mm, normal (0,0,-1), area 91.3mm2, adj f84,f85,f86,f87,f88,f89,f90,f91
  f113: plane 9.34x6.53mm, normal (0,0,-1), area 53.6mm2, adj f53,f54,f55,f56,f57,f58,f66
PART E: same geometry as D
PLACE A t=(-83.17,-0.89,5.83)mm
PLACE B rot(axis=(0,1,0),180deg) t=(86.83,-0.89,6.83)mm
PLACE C t=(1.83,-0.89,-11.67)mm fixed
PLACE D rot(axis=(-1,0,0),70deg) t=(-102.78,-89.16,-29.67)mm
PLACE E rot(axis=(-1,0,0),70deg) t=(110.71,-89.16,-29.67)mm
MATE fastened A.f69 <-> C.f4  axis (0,0,-1) through (-168.17,89.11,5.83)mm
MATE planar D.f4 <-> C.f2  axis (0,1,0) through (-131.78,-90.89,-2.92)mm
MATE fastened B.f130 <-> C.f4  axis (0,0,-1) through (171.83,89.11,5.83)mm
MATE planar E.f4 <-> C.f2  axis (0,1,0) through (139.71,-90.89,-2.92)mm
